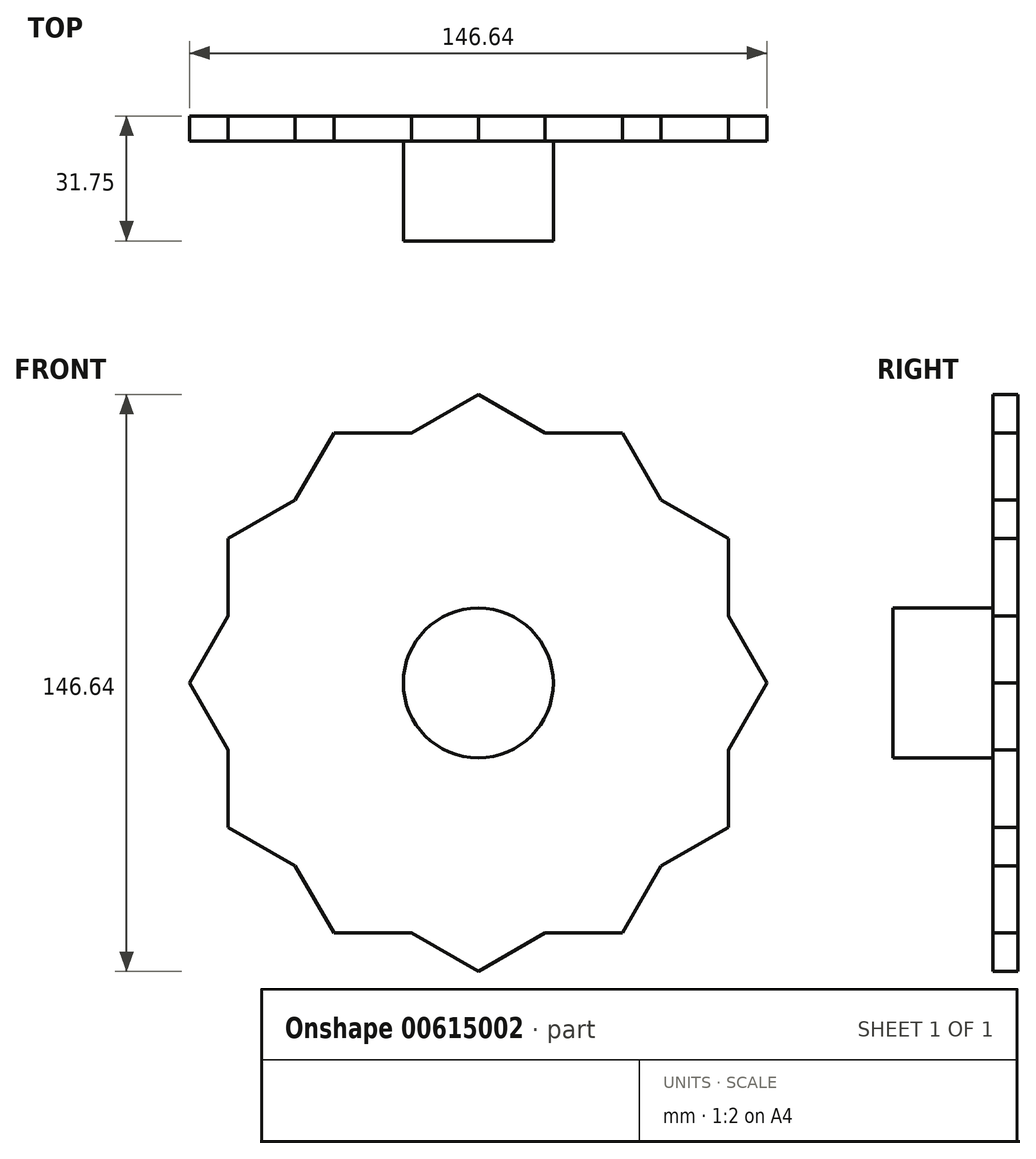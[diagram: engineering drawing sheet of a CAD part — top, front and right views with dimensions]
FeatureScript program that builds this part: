
annotation { "Feature Type Name" : "Feature", "Feature Type Description" : "" }
export const myFeature = defineFeature(function(context is Context, id is Id, definition is map)
    precondition{}
    {
        {
            var Q0;
            Q0=qCreatedBy(makeId("Front.planeOp"),FACE);
            var sketch = newSketch(context, id + "F0", { "sketchPlane" : qUnion([Q0])});
            skCircle(sketch, "E0", {"center": v(0, 0) * mm, "radius": 19.05 * mm});
            skCircle(sketch, "E1.cCircle", {"center": v(0, 0) * mm, "radius": 63.5 * mm, "construction": true});
            skLineSegment(sketch, "E1.0", {"start": v(-36.66, 63.5) * mm, "end": v(36.66, 63.5) * mm});
            skLineSegment(sketch, "E1.1", {"start": v(36.66, 63.5) * mm, "end": v(73.32, 0) * mm});
            skLineSegment(sketch, "E1.2", {"start": v(73.32, 0) * mm, "end": v(36.66, -63.5) * mm});
            skLineSegment(sketch, "E1.3", {"start": v(36.66, -63.5) * mm, "end": v(-36.66, -63.5) * mm});
            skLineSegment(sketch, "E1.4", {"start": v(-36.66, -63.5) * mm, "end": v(-73.32, 0) * mm});
            skLineSegment(sketch, "E1.5", {"start": v(-73.32, 0) * mm, "end": v(-36.66, 63.5) * mm});
            skPoint(sketch, "E1.0.midPoint", {"position": v(0, 63.5) * mm});
            skCircle(sketch, "E2.cCircle", {"center": v(0, 0) * mm, "radius": 73.32 * mm, "construction": true});
            skLineSegment(sketch, "E2.0", {"start": v(0, 73.32) * mm, "end": v(63.5, 36.66) * mm});
            skLineSegment(sketch, "E2.1", {"start": v(63.5, 36.66) * mm, "end": v(63.5, -36.66) * mm});
            skLineSegment(sketch, "E2.2", {"start": v(63.5, -36.66) * mm, "end": v(0, -73.32) * mm});
            skLineSegment(sketch, "E2.3", {"start": v(0, -73.32) * mm, "end": v(-63.5, -36.66) * mm});
            skLineSegment(sketch, "E2.4", {"start": v(-63.5, -36.66) * mm, "end": v(-63.5, 36.66) * mm});
            skLineSegment(sketch, "E2.5", {"start": v(-63.5, 36.66) * mm, "end": v(0, 73.32) * mm});
            skSolve(sketch);
        }
        {
            var Q0;
            {var subQ0=sQuery(id+"F0.wireOp",EDGE,"E1.1");var subQ1=sQuery(id+"F0.wireOp",EDGE,"E1.0");var subQ2=makeQuery(id+"F0.imprint","INTERSECT",VERTEX,{"derivedFrom":[subQ1,subQ0]});Q0=makeQuery(id+"F0.imprint","IMPRINT",FACE,{"disambiguationData":[TD([[makeQuery(id+"F0.imprint","IMPRINT",EDGE,{"disambiguationData":[TD([[subQ2,1.0]])],"derivedFrom":subQ1}),-1.0]])]});}
            var Q1;
            {var subQ0=sQuery(id+"F0.wireOp",EDGE,"E1.3");var subQ1=sQuery(id+"F0.wireOp",EDGE,"E1.2");var subQ2=makeQuery(id+"F0.imprint","INTERSECT",VERTEX,{"derivedFrom":[subQ1,subQ0]});Q1=makeQuery(id+"F0.imprint","IMPRINT",FACE,{"disambiguationData":[TD([[makeQuery(id+"F0.imprint","IMPRINT",EDGE,{"disambiguationData":[TD([[subQ2,1.0]])],"derivedFrom":subQ1}),-1.0]])]});}
            var Q2;
            {var subQ0=sQuery(id+"F0.wireOp",EDGE,"E2.1");var subQ1=sQuery(id+"F0.wireOp",EDGE,"E1.2");var subQ2=makeQuery(id+"F0.imprint","INTERSECT",VERTEX,{"derivedFrom":[subQ1,subQ0]});Q2=makeQuery(id+"F0.imprint","IMPRINT",FACE,{"disambiguationData":[TD([[makeQuery(id+"F0.imprint","IMPRINT",EDGE,{"disambiguationData":[TD([[subQ2,-1.0]])],"derivedFrom":subQ1}),1.0]])]});}
            var Q3;
            {var subQ0=sQuery(id+"F0.wireOp",EDGE,"E1.5");var subQ1=sQuery(id+"F0.wireOp",EDGE,"E1.0");var subQ2=makeQuery(id+"F0.imprint","INTERSECT",VERTEX,{"derivedFrom":[subQ1,subQ0]});Q3=makeQuery(id+"F0.imprint","IMPRINT",FACE,{"disambiguationData":[TD([[makeQuery(id+"F0.imprint","IMPRINT",EDGE,{"disambiguationData":[TD([[subQ2,-1.0]])],"derivedFrom":subQ1}),-1.0]])]});}
            var Q4;
            Q4=makeQuery(id+"F0.imprint","IMPRINT",FACE,{"disambiguationData":[TD([[makeQuery(id+"F0.imprint","IMPRINT",EDGE,{"derivedFrom":sQuery(id+"F0.wireOp",EDGE,"E0")}),1.0]])]});
            var Q5;
            {var subQ0=sQuery(id+"F0.wireOp",EDGE,"E1.2");var subQ1=sQuery(id+"F0.wireOp",EDGE,"E1.1");var subQ2=makeQuery(id+"F0.imprint","INTERSECT",VERTEX,{"derivedFrom":[subQ1,subQ0]});Q5=makeQuery(id+"F0.imprint","IMPRINT",FACE,{"disambiguationData":[TD([[makeQuery(id+"F0.imprint","IMPRINT",EDGE,{"disambiguationData":[TD([[subQ2,1.0]])],"derivedFrom":subQ1}),-1.0]])]});}
            var Q6;
            {var subQ0=sQuery(id+"F0.wireOp",EDGE,"E2.0");var subQ1=sQuery(id+"F0.wireOp",EDGE,"E1.1");var subQ2=makeQuery(id+"F0.imprint","INTERSECT",VERTEX,{"derivedFrom":[subQ1,subQ0]});Q6=makeQuery(id+"F0.imprint","IMPRINT",FACE,{"disambiguationData":[TD([[makeQuery(id+"F0.imprint","IMPRINT",EDGE,{"disambiguationData":[TD([[subQ2,-1.0]])],"derivedFrom":subQ1}),1.0]])]});}
            var Q7;
            Q7=makeQuery(id+"F0.imprint","IMPRINT",FACE,{"disambiguationData":[TD([[makeQuery(id+"F0.imprint","IMPRINT",EDGE,{"derivedFrom":sQuery(id+"F0.wireOp",EDGE,"E0")}),-1.0]])]});
            var Q8;
            {var subQ0=sQuery(id+"F0.wireOp",EDGE,"E2.2");var subQ1=sQuery(id+"F0.wireOp",EDGE,"E1.3");var subQ2=makeQuery(id+"F0.imprint","INTERSECT",VERTEX,{"derivedFrom":[subQ1,subQ0]});Q8=makeQuery(id+"F0.imprint","IMPRINT",FACE,{"disambiguationData":[TD([[makeQuery(id+"F0.imprint","IMPRINT",EDGE,{"disambiguationData":[TD([[subQ2,-1.0]])],"derivedFrom":subQ1}),1.0]])]});}
            var Q9;
            {var subQ0=sQuery(id+"F0.wireOp",EDGE,"E1.4");var subQ1=sQuery(id+"F0.wireOp",EDGE,"E1.3");var subQ2=makeQuery(id+"F0.imprint","INTERSECT",VERTEX,{"derivedFrom":[subQ1,subQ0]});Q9=makeQuery(id+"F0.imprint","IMPRINT",FACE,{"disambiguationData":[TD([[makeQuery(id+"F0.imprint","IMPRINT",EDGE,{"disambiguationData":[TD([[subQ2,1.0]])],"derivedFrom":subQ1}),-1.0]])]});}
            var Q10;
            {var subQ0=sQuery(id+"F0.wireOp",EDGE,"E2.3");var subQ1=sQuery(id+"F0.wireOp",EDGE,"E1.4");var subQ2=makeQuery(id+"F0.imprint","INTERSECT",VERTEX,{"derivedFrom":[subQ1,subQ0]});Q10=makeQuery(id+"F0.imprint","IMPRINT",FACE,{"disambiguationData":[TD([[makeQuery(id+"F0.imprint","IMPRINT",EDGE,{"disambiguationData":[TD([[subQ2,-1.0]])],"derivedFrom":subQ1}),1.0]])]});}
            var Q11;
            {var subQ0=sQuery(id+"F0.wireOp",EDGE,"E1.5");var subQ1=sQuery(id+"F0.wireOp",EDGE,"E1.4");var subQ2=makeQuery(id+"F0.imprint","INTERSECT",VERTEX,{"derivedFrom":[subQ1,subQ0]});Q11=makeQuery(id+"F0.imprint","IMPRINT",FACE,{"disambiguationData":[TD([[makeQuery(id+"F0.imprint","IMPRINT",EDGE,{"disambiguationData":[TD([[subQ2,1.0]])],"derivedFrom":subQ1}),-1.0]])]});}
            var Q12;
            {var subQ0=sQuery(id+"F0.wireOp",EDGE,"E2.4");var subQ1=sQuery(id+"F0.wireOp",EDGE,"E1.5");var subQ2=makeQuery(id+"F0.imprint","INTERSECT",VERTEX,{"derivedFrom":[subQ1,subQ0]});Q12=makeQuery(id+"F0.imprint","IMPRINT",FACE,{"disambiguationData":[TD([[makeQuery(id+"F0.imprint","IMPRINT",EDGE,{"disambiguationData":[TD([[subQ2,-1.0]])],"derivedFrom":subQ1}),1.0]])]});}
            var Q13;
            {var subQ0=sQuery(id+"F0.wireOp",EDGE,"E2.5");var subQ1=sQuery(id+"F0.wireOp",EDGE,"E1.0");var subQ2=makeQuery(id+"F0.imprint","INTERSECT",VERTEX,{"derivedFrom":[subQ1,subQ0]});Q13=makeQuery(id+"F0.imprint","IMPRINT",FACE,{"disambiguationData":[TD([[makeQuery(id+"F0.imprint","IMPRINT",EDGE,{"disambiguationData":[TD([[subQ2,-1.0]])],"derivedFrom":subQ1}),1.0]])]});}
            extrude(context, id + "F1", {"entities" : qUnion([Q0, Q1, Q2, Q3, Q4, Q5, Q6, Q7, Q8, Q9, Q10, Q11, Q12, Q13]), "oppositeDirection" : true, "depth" : 6.35 * mm, "offsetDistance" : 25.4 * mm});
        }
        {
            var Q0;
            Q0=makeQuery(id+"F0.imprint","IMPRINT",FACE,{"disambiguationData":[TD([[makeQuery(id+"F0.imprint","IMPRINT",EDGE,{"derivedFrom":sQuery(id+"F0.wireOp",EDGE,"E0")}),1.0]])]});
            extrude(context, id + "F2", {"entities" : qUnion([Q0]), "operationType" : NewBodyOperationType.ADD, "depth" : 25.4 * mm, "offsetDistance" : 25.4 * mm});
        }
    });
